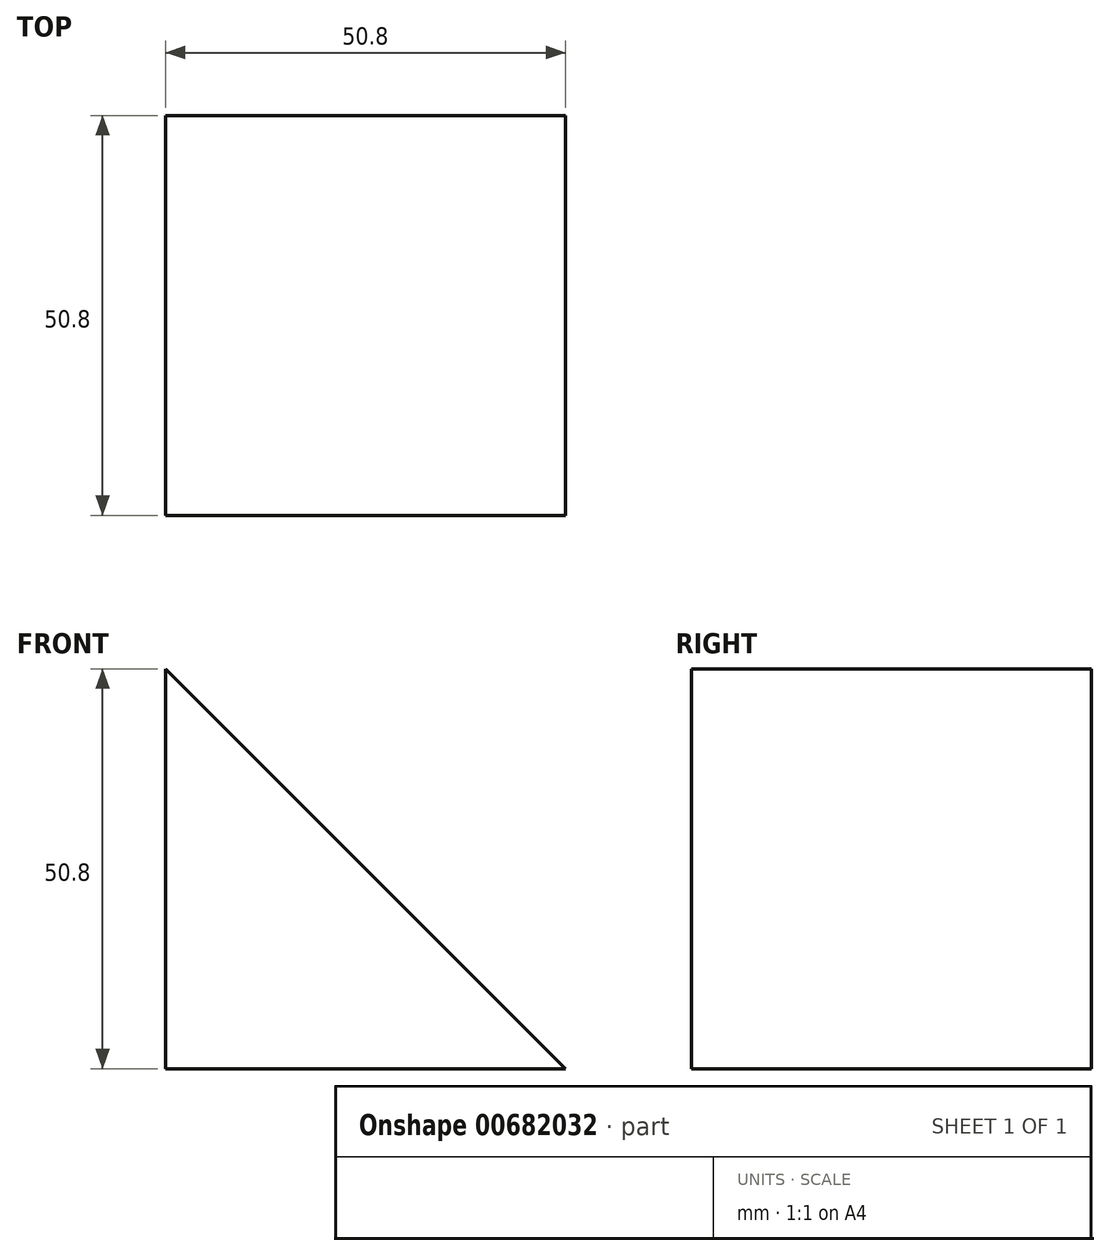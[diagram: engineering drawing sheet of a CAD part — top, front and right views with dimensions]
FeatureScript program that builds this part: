
annotation { "Feature Type Name" : "Feature", "Feature Type Description" : "" }
export const myFeature = defineFeature(function(context is Context, id is Id, definition is map)
    precondition{}
    {
        {
            var Q0;
            Q0=qCreatedBy(makeId("Front.planeOp"),FACE);
            var sketch = newSketch(context, id + "F0", { "sketchPlane" : qUnion([Q0])});
            skLineSegment(sketch, "E0", {"start": v(-50.7, 50.8) * mm, "end": v(-50.7, 0) * mm});
            skLineSegment(sketch, "E1", {"start": v(-50.7, 0) * mm, "end": v(0.1, 0) * mm});
            skLineSegment(sketch, "E2", {"start": v(-50.7, 50.8) * mm, "end": v(0.1, 0) * mm});
            skSolve(sketch);
        }
        {
            var Q0;
            Q0 = qSketchRegion(id + "F0", true);
            extrude(context, id + "F1", {"entities" : qUnion([Q0]), "depth" : 50.8 * mm, "offsetDistance" : 25.4 * mm});
        }
    });
